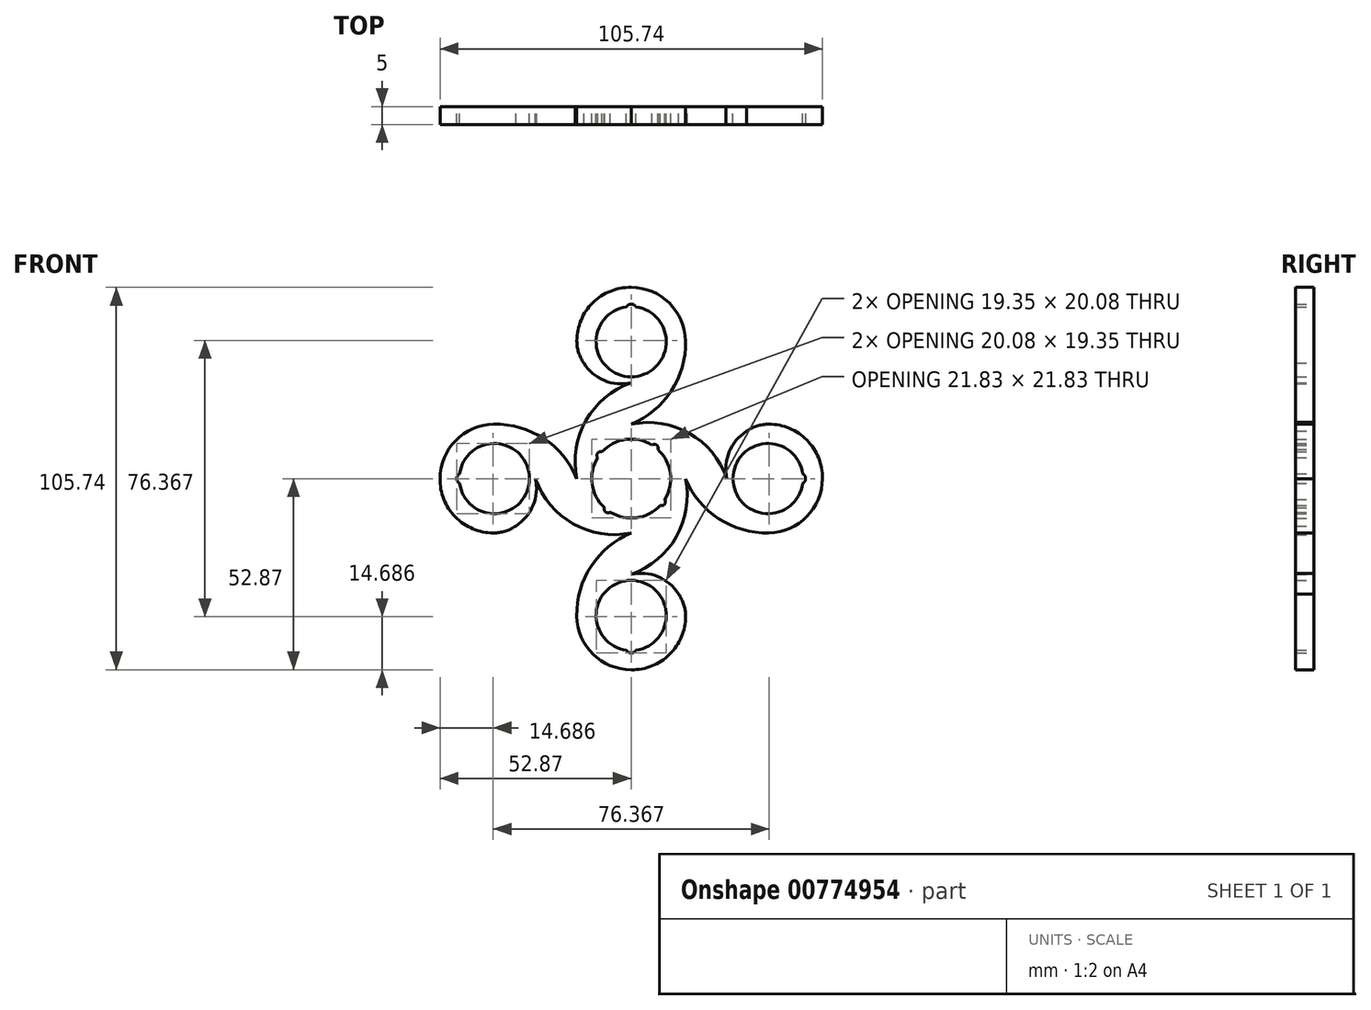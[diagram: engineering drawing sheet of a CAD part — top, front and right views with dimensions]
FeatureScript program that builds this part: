
annotation { "Feature Type Name" : "Feature", "Feature Type Description" : "" }
export const myFeature = defineFeature(function(context is Context, id is Id, definition is map)
    precondition{}
    {
        {
            var Q0;
            Q0=qCreatedBy(makeId("Front.planeOp"),FACE);
            var sketch = newSketch(context, id + "F0", { "sketchPlane" : qUnion([Q0])});
            skArc(sketch, "E0", {"start": v(5.78, 9.27) * mm, "mid": v(-1.47, 10.83) * mm, "end": v(-8.04, 7.4) * mm});
            skLineSegment(sketch, "E1", {"start": v(0, 0) * mm, "end": v(0, 37.84) * mm, "construction": true});
            skArc(sketch, "E2", {"start": v(-1.32, 47.45) * mm, "mid": v(0, 28.14) * mm, "end": v(1.32, 47.45) * mm});
            skArc(sketch, "E3", {"start": v(15.03, 38.06) * mm, "mid": v(0, 52.87) * mm, "end": v(-15.03, 38.06) * mm, "construction": true});
            skArc(sketch, "E4", {"start": v(0, 52.87) * mm, "mid": v(-10.61, 48.6) * mm, "end": v(-15.03, 38.06) * mm});
            skArc(sketch, "E5", {"start": v(0, 15.03) * mm, "mid": v(11.08, 24.21) * mm, "end": v(15.03, 38.06) * mm});
            skArc(sketch, "E6", {"start": v(15.03, 38.06) * mm, "mid": v(10.53, 48.53) * mm, "end": v(0, 52.87) * mm});
            skArc(sketch, "E7.1.0", {"start": v(-38.06, 15.03) * mm, "mid": v(-52.87, 0) * mm, "end": v(-38.06, -15.03) * mm, "construction": true});
            skArc(sketch, "E7.1.1", {"start": v(-47.45, -1.32) * mm, "mid": v(-28.14, 0) * mm, "end": v(-47.45, 1.32) * mm});
            skArc(sketch, "E7.1.3", {"start": v(-38.06, 15.03) * mm, "mid": v(-48.53, 10.53) * mm, "end": v(-52.87, 0) * mm});
            skArc(sketch, "E7.1.4", {"start": v(-52.87, 0) * mm, "mid": v(-48.6, -10.61) * mm, "end": v(-38.06, -15.03) * mm});
            skArc(sketch, "E7.1.5", {"start": v(-38.06, -15.03) * mm, "mid": v(-34.82, -14.53) * mm, "end": v(-31.89, -13.09) * mm});
            skArc(sketch, "E7.1.6", {"start": v(-15.03, 0) * mm, "mid": v(-24.21, 11.08) * mm, "end": v(-38.06, 15.03) * mm});
            skArc(sketch, "E7.2.0", {"start": v(-15.03, -38.06) * mm, "mid": v(0, -52.87) * mm, "end": v(15.03, -38.06) * mm, "construction": true});
            skArc(sketch, "E7.2.1", {"start": v(1.32, -47.45) * mm, "mid": v(0, -28.14) * mm, "end": v(-1.32, -47.45) * mm});
            skArc(sketch, "E7.2.3", {"start": v(-15.03, -38.06) * mm, "mid": v(-10.53, -48.53) * mm, "end": v(0, -52.87) * mm});
            skArc(sketch, "E7.2.4", {"start": v(0, -52.87) * mm, "mid": v(10.61, -48.6) * mm, "end": v(15.03, -38.06) * mm});
            skArc(sketch, "E7.2.5", {"start": v(15.03, -38.06) * mm, "mid": v(14.53, -34.82) * mm, "end": v(13.09, -31.89) * mm});
            skArc(sketch, "E7.2.6", {"start": v(0, -15.03) * mm, "mid": v(-11.08, -24.21) * mm, "end": v(-15.03, -38.06) * mm});
            skPoint(sketch, "E8.orphan", {"position": v(0, 28.14) * mm});
            skArc(sketch, "E9.4.3.0", {"start": v(47.45, 1.32) * mm, "mid": v(28.14, 0) * mm, "end": v(47.45, -1.32) * mm});
            skArc(sketch, "E9.8.3.0", {"start": v(38.06, -15.03) * mm, "mid": v(48.54, -10.55) * mm, "end": v(52.87, 0) * mm, "construction": true});
            skArc(sketch, "E9.10.3.0", {"start": v(38.06, -15.03) * mm, "mid": v(48.53, -10.53) * mm, "end": v(52.87, 0) * mm});
            skArc(sketch, "E9.14.3.0", {"start": v(52.87, 0) * mm, "mid": v(48.6, 10.61) * mm, "end": v(38.06, 15.03) * mm});
            skArc(sketch, "E9.18.3.0", {"start": v(38.06, 15.03) * mm, "mid": v(34.82, 14.53) * mm, "end": v(31.89, 13.09) * mm});
            skPoint(sketch, "E9.21.3.0", {"position": v(28.14, 0) * mm});
            skArc(sketch, "E9.22.3.0", {"start": v(15.03, 0) * mm, "mid": v(24.21, -11.08) * mm, "end": v(38.06, -15.03) * mm});
            skPoint(sketch, "E10.center.orphan", {"position": v(-4.24, 38.06) * mm});
            skArc(sketch, "E11", {"start": v(31.89, 13.09) * mm, "mid": v(26.2, 2.03) * mm, "end": v(32.98, -8.4) * mm});
            skArc(sketch, "E12", {"start": v(26.47, 0) * mm, "mid": v(16.06, 12.5) * mm, "end": v(0, 15.03) * mm});
            skPoint(sketch, "E13.orphan", {"position": v(22.24, 0) * mm});
            skArc(sketch, "E14.1.0", {"start": v(-15.03, 38.06) * mm, "mid": v(-14.53, 34.82) * mm, "end": v(-13.09, 31.89) * mm});
            skPoint(sketch, "E14.1.2", {"position": v(0, 22.24) * mm});
            skArc(sketch, "E14.1.3", {"start": v(-13.09, 31.89) * mm, "mid": v(-2.03, 26.2) * mm, "end": v(8.4, 32.98) * mm});
            skArc(sketch, "E14.1.6", {"start": v(0, 26.47) * mm, "mid": v(-12.5, 16.06) * mm, "end": v(-15.03, 0) * mm});
            skPoint(sketch, "E14.2.2", {"position": v(-22.24, 0) * mm});
            skArc(sketch, "E14.2.3", {"start": v(-31.89, -13.09) * mm, "mid": v(-26.2, -2.03) * mm, "end": v(-32.98, 8.4) * mm});
            skPoint(sketch, "E14.2.4", {"position": v(-28.14, 0) * mm});
            skArc(sketch, "E14.2.6", {"start": v(-26.47, 0) * mm, "mid": v(-16.06, -12.5) * mm, "end": v(0, -15.03) * mm});
            skPoint(sketch, "E14.3.2", {"position": v(0, -22.24) * mm});
            skArc(sketch, "E14.3.3", {"start": v(13.09, -31.89) * mm, "mid": v(2.03, -26.2) * mm, "end": v(-8.4, -32.98) * mm});
            skPoint(sketch, "E14.3.4", {"position": v(0, -28.14) * mm});
            skArc(sketch, "E14.3.6", {"start": v(0, -26.47) * mm, "mid": v(12.5, -16.06) * mm, "end": v(15.03, 0) * mm});
            skPoint(sketch, "E15.end.orphan", {"position": v(9.7, 37.84) * mm});
            skPoint(sketch, "E16.end.orphan", {"position": v(-15.03, 0) * mm});
            skArc(sketch, "E17", {"start": v(7.4, 8.04) * mm, "mid": v(7.05, 9.27) * mm, "end": v(5.78, 9.27) * mm});
            skArc(sketch, "E18.1.0", {"start": v(-8.04, 7.4) * mm, "mid": v(-9.27, 7.05) * mm, "end": v(-9.27, 5.78) * mm});
            skArc(sketch, "E18.2.0", {"start": v(-7.4, -8.04) * mm, "mid": v(-7.05, -9.27) * mm, "end": v(-5.78, -9.27) * mm});
            skArc(sketch, "E18.3.0", {"start": v(8.04, -7.4) * mm, "mid": v(9.27, -7.05) * mm, "end": v(9.27, -5.78) * mm});
            skArc(sketch, "E19.trimOffspring", {"start": v(-9.27, 5.78) * mm, "mid": v(-10.83, -1.47) * mm, "end": v(-7.4, -8.04) * mm});
            skArc(sketch, "E20.trimOffspring", {"start": v(9.27, -5.78) * mm, "mid": v(10.83, 1.47) * mm, "end": v(7.4, 8.04) * mm});
            skArc(sketch, "E21.trimOffspring", {"start": v(-5.78, -9.27) * mm, "mid": v(1.47, -10.83) * mm, "end": v(8.04, -7.4) * mm});
            skArc(sketch, "E22", {"start": v(1.32, 47.45) * mm, "mid": v(0, 48.23) * mm, "end": v(-1.32, 47.45) * mm});
            skArc(sketch, "E23.1.0", {"start": v(-47.45, 1.32) * mm, "mid": v(-48.23, 0) * mm, "end": v(-47.45, -1.32) * mm});
            skArc(sketch, "E23.2.0", {"start": v(-1.32, -47.45) * mm, "mid": v(0, -48.23) * mm, "end": v(1.32, -47.45) * mm});
            skArc(sketch, "E23.3.0", {"start": v(47.45, -1.32) * mm, "mid": v(48.23, 0) * mm, "end": v(47.45, 1.32) * mm});
            skSolve(sketch);
        }
        {
            var Q0;
            Q0=makeQuery(id+"F0.imprint","IMPRINT",FACE,{"disambiguationData":[TD([[makeQuery(id+"F0.imprint","IMPRINT",EDGE,{"derivedFrom":sQuery(id+"F0.wireOp",EDGE,"E0")}),-1.0]])]});
            extrude(context, id + "F1", {"entities" : qUnion([Q0]), "depth" : 5 * mm, "offsetDistance" : 25 * mm});
        }
    });
